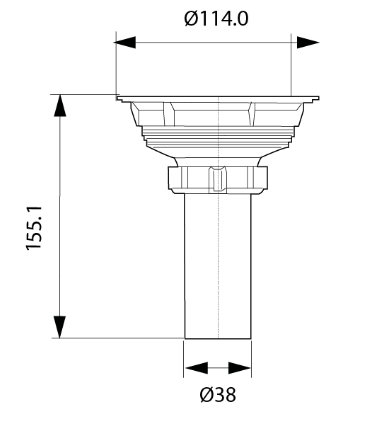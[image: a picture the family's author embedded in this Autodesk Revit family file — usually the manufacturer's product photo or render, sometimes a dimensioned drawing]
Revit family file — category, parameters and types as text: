
# Revit family: 135106851_Mueble Pontus Vital 60 cm con Lavamanos
name_source: partatom
category: Furniture
units: mm (PartAtom-declared; Revit-internal decimal feet)

## family parameters
Always vertical = Yes
Cut with Voids When Loaded = No
OmniClass Number = 23.31.13.11
OmniClass Title = Single Sinks
Room Calculation Point = No
Shared = No
Work Plane-Based = No

## types (1)
- 135106851_Mueble Pontus Vital 60 cm con Lavamanos
    Acabado = Corona_Plastico_Taupe
    Alto = 764 mm  [stored 2.50656 ft]
    Ancho = 600 mm
    Creado por = IDD
    Description = Línea de Muebles Pontus Vital diseño compacto que se adapta a la gran mayoría de
espacios disponibles.
· Diseño de apertura cómodo.
· Máxima capacidad de almacenamiento.
· Lavamanos 100% en porcelana con superficie amplia de apoyo.
· Resistentes a la humedad.
    Fecha de creación = 30/07/2020
    Garantía = 5 Años  (Madera)
    Garantía Herraje = 1 Años
    Longitud = 450 mm  [stored 1.47638 ft]
    Manufacturer = Corona
    Material = Corona_Madera_Coñac
    Model = Pontus Vital 60
    Peso Bruto aprox = 25,6 lb (11,6 kg).
    Peso Neto aprox = 24,0 lb (10,9 kg).
    Resistencia a la humedad = 8%.
    Resistencia al rayado = 700 ciclos
    URL = https://corona.co

note: [stored X ft] marks values corroborated as IEEE doubles in the binary element streams (Revit-internal decimal feet)

## geometry (parser evidence)
native form markers: Sweep x10
no freeform markers — native parametric forms only
